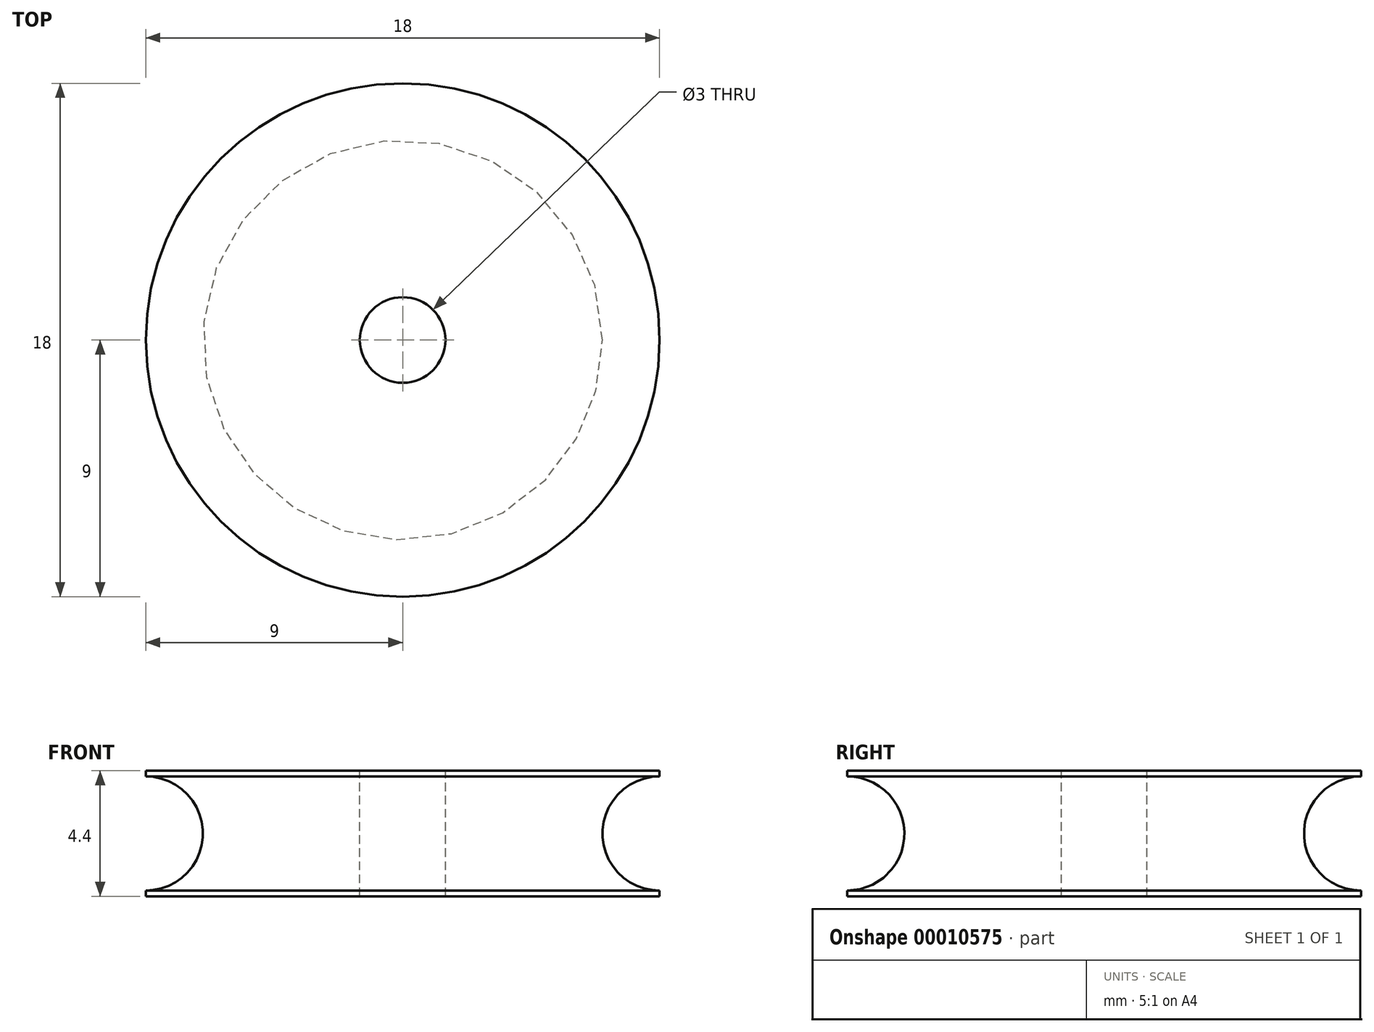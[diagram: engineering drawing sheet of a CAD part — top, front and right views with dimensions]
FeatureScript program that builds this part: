
annotation { "Feature Type Name" : "Feature", "Feature Type Description" : "" }
export const myFeature = defineFeature(function(context is Context, id is Id, definition is map)
    precondition{}
    {
        {
            var Q0;
            Q0=qCreatedBy(makeId("Front.planeOp"),FACE);
            var sketch = newSketch(context, id + "F0", { "sketchPlane" : qUnion([Q0])});
            skLineSegment(sketch, "E0", {"start": v(0, 3.55) * mm, "end": v(0, -2.82) * mm, "construction": true});
            skLineSegment(sketch, "E1", {"start": v(0, 0) * mm, "end": v(9, 0) * mm, "construction": true});
            skArc(sketch, "E2", {"start": v(9, 2) * mm, "mid": v(7, 0) * mm, "end": v(9, -2) * mm});
            skLineSegment(sketch, "E3.bottom", {"start": v(9, 2.2) * mm, "end": v(1.5, 2.2) * mm});
            skLineSegment(sketch, "E3.top", {"start": v(9, -2.2) * mm, "end": v(1.5, -2.2) * mm});
            skLineSegment(sketch, "E3.left", {"start": v(9, 2.2) * mm, "end": v(9, 2) * mm});
            skLineSegment(sketch, "E3.right", {"start": v(1.5, 2.2) * mm, "end": v(1.5, -2.2) * mm});
            skLineSegment(sketch, "E4.trimOffspring", {"start": v(9, -2) * mm, "end": v(9, -2.2) * mm});
            skSolve(sketch);
        }
        {
            var Q0;
            Q0 = qSketchRegion(id + "F0", true);
            var Q1;
            Q1=sQuery(id+"F0.wireOp",EDGE,"E0");
            revolve(context, id + "F1", {"entities" : qUnion([Q0]), "axis" : qUnion([Q1]), "revolveType" : RevolveType.FULL});
        }
    });
